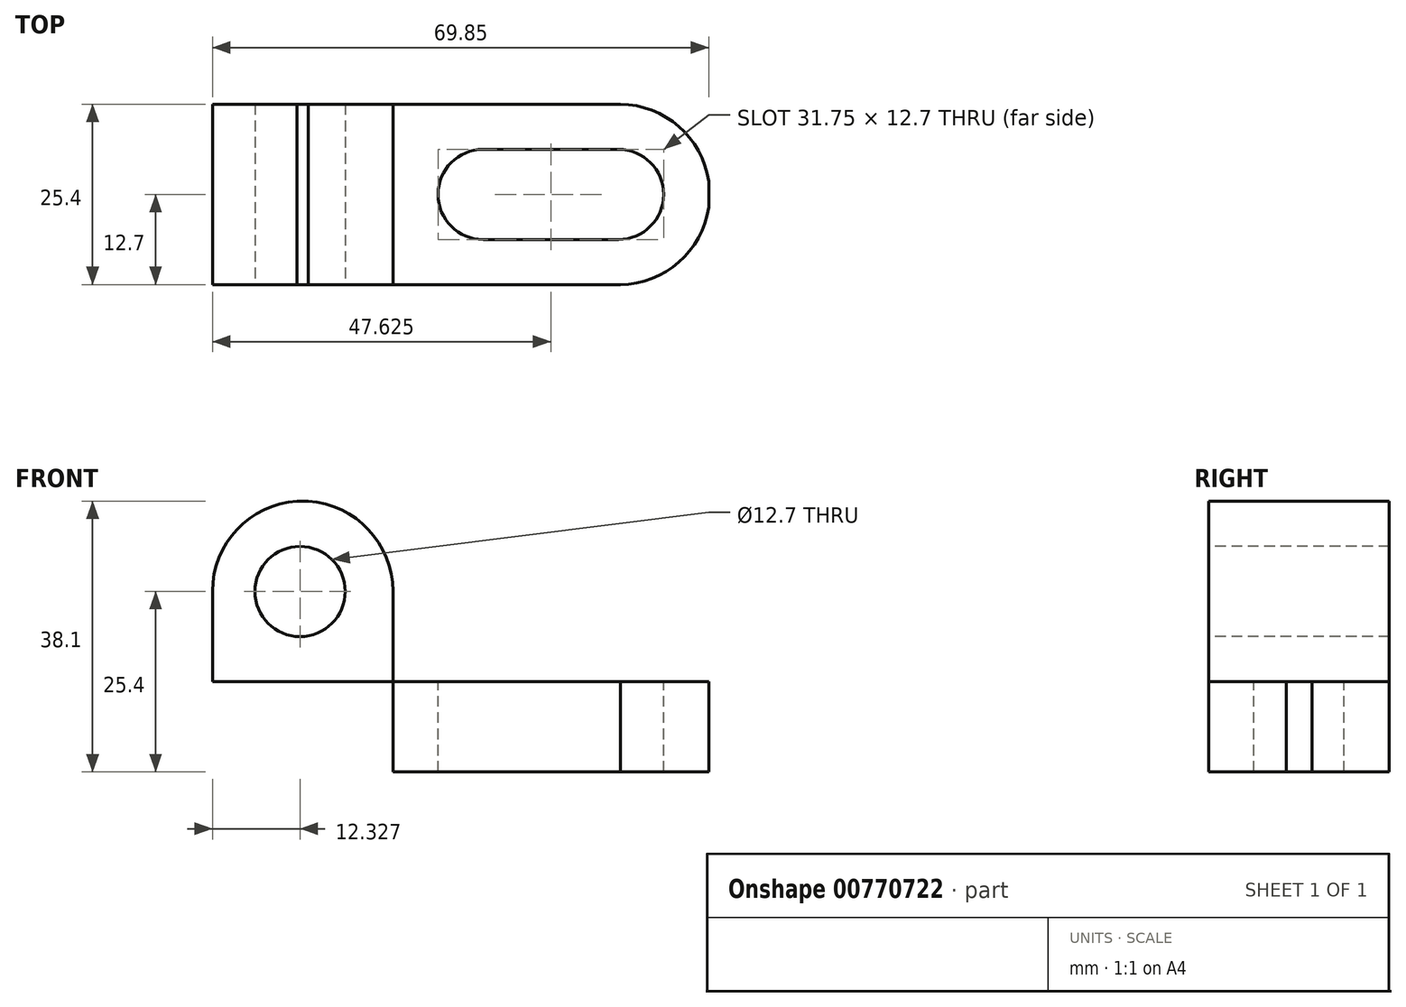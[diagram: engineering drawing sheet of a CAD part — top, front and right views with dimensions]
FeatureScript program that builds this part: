
annotation { "Feature Type Name" : "Feature", "Feature Type Description" : "" }
export const myFeature = defineFeature(function(context is Context, id is Id, definition is map)
    precondition{}
    {
        {
            var Q0;
            Q0=qCreatedBy(makeId("Front.planeOp"),FACE);
            var sketch = newSketch(context, id + "F0", { "sketchPlane" : qUnion([Q0])});
            skLineSegment(sketch, "E0.bottom", {"start": v(0, 0) * mm, "end": v(25.4, 0) * mm});
            skLineSegment(sketch, "E0.top", {"start": v(0, 38.1) * mm, "end": v(25.4, 38.1) * mm});
            skLineSegment(sketch, "E0.left", {"start": v(0, 0) * mm, "end": v(0, 38.1) * mm});
            skLineSegment(sketch, "E0.right", {"start": v(25.4, 0) * mm, "end": v(25.4, 38.1) * mm});
            skLineSegment(sketch, "E1.bottom", {"start": v(0, 0) * mm, "end": v(69.85, 0) * mm});
            skLineSegment(sketch, "E1.top", {"start": v(0, 12.7) * mm, "end": v(69.85, 12.7) * mm});
            skLineSegment(sketch, "E1.left", {"start": v(0, 0) * mm, "end": v(0, 12.7) * mm});
            skLineSegment(sketch, "E1.right", {"start": v(69.85, 0) * mm, "end": v(69.85, 12.7) * mm});
            skSolve(sketch);
        }
        {
            var Q0;
            {var subQ0=sQuery(id+"F0.wireOp",EDGE,"E0.top");Q0=makeQuery(id+"F0.imprint","IMPRINT",FACE,{"disambiguationData":[TD([[makeQuery(id+"F0.imprint","IMPRINT",EDGE,{"derivedFrom":subQ0}),-1.0]])]});}
            var Q1;
            {var subQ5=sQuery(id+"F0.wireOp",EDGE,"E1.left");Q1=makeQuery(id+"F0.imprint","IMPRINT",FACE,{"disambiguationData":[TD([[makeQuery(id+"F0.imprint","IMPRINT",EDGE,{"derivedFrom":subQ5}),-1.0]])]});}
            var Q2;
            {var subQ5=sQuery(id+"F0.wireOp",EDGE,"E1.right");Q2=makeQuery(id+"F0.imprint","IMPRINT",FACE,{"disambiguationData":[TD([[makeQuery(id+"F0.imprint","IMPRINT",EDGE,{"derivedFrom":subQ5}),1.0]])]});}
            extrude(context, id + "F1", {"entities" : qUnion([Q0, Q1, Q2]), "depth" : 25.4 * mm});
        }
        {
            var Q0;
            Q0=makeQuery(id+"F1.opExtrude","CAP_FACE",FACE,{"disambiguationData":[OSD([sQuery(id+"F0.wireOp",EDGE,"E0.top"),sQuery(id+"F0.wireOp",EDGE,"E0.left"),sQuery(id+"F0.wireOp",EDGE,"E0.right"),sQuery(id+"F0.wireOp",EDGE,"E1.bottom"),sQuery(id+"F0.wireOp",EDGE,"E1.top"),sQuery(id+"F0.wireOp",EDGE,"E1.left"),sQuery(id+"F0.wireOp",EDGE,"E1.right")])],"isStart":false});
            var sketch = newSketch(context, id + "F2", { "sketchPlane" : qUnion([Q0])});
            skCircle(sketch, "E2", {"center": v(12.33, 25.4) * mm, "radius": 6.35 * mm});
            skArc(sketch, "E3", {"start": v(25.4, 25.4) * mm, "mid": v(12.7, 38.12) * mm, "end": v(0, 25.4) * mm});
            skSolve(sketch);
        }
        {
            var Q0;
            Q0=qSketchRegion(id+"F2",true);
            var Q1;
            {var subQ0=sQuery(id+"F2.wireOp",EDGE,"E3");var subQ1=makeQuery(id+"F1.opExtrude","CAP_EDGE",EDGE,{"disambiguationData":[OSD([sQuery(id+"F0.wireOp",EDGE,"E0.right")])],"isStart":false});var subQ2=makeQuery(id+"F2.imprint","INTERSECT",VERTEX,{"derivedFrom":[subQ1,subQ0]});Q1=makeQuery(id+"F2.imprint","IMPRINT",FACE,{"disambiguationData":[TD([[makeQuery(id+"F2.imprint","IMPRINT",EDGE,{"disambiguationData":[TD([[subQ2,-1.0]])],"derivedFrom":subQ0}),-1.0]])]});}
            var Q2;
            {var subQ0=sQuery(id+"F2.wireOp",EDGE,"E3");var subQ3=makeQuery(id+"F1.opExtrude","CAP_EDGE",EDGE,{"disambiguationData":[OSD([sQuery(id+"F0.wireOp",EDGE,"E0.top")])],"isStart":false});var subQ4=makeQuery(id+"F2.imprint","INTERSECT",VERTEX,{"disambiguationData":[OD(1.0)],"derivedFrom":[subQ3,subQ0]});Q2=makeQuery(id+"F2.imprint","IMPRINT",FACE,{"disambiguationData":[TD([[makeQuery(id+"F2.imprint","IMPRINT",EDGE,{"disambiguationData":[TD([[subQ4,-1.0]])],"derivedFrom":subQ0}),-1.0]])]});}
            extrude(context, id + "F3", {"entities" : qUnion([Q0, Q1, Q2]), "operationType" : NewBodyOperationType.REMOVE, "oppositeDirection" : true, "depth" : 25.4 * mm});
        }
        {
            var Q0;
            Q0=makeQuery(id+"F1.opExtrude","SWEPT_FACE",FACE,{"disambiguationData":[OSD([sQuery(id+"F0.wireOp",EDGE,"E1.top")])]});
            var sketch = newSketch(context, id + "F4", { "sketchPlane" : qUnion([Q0])});
            skCircle(sketch, "E4", {"center": v(38.1, -12.7) * mm, "radius": 6.35 * mm});
            skCircle(sketch, "E5", {"center": v(57.15, -12.7) * mm, "radius": 6.35 * mm});
            skLineSegment(sketch, "E6", {"start": v(38.1, -19.05) * mm, "end": v(57.15, -19.05) * mm});
            skLineSegment(sketch, "E7", {"start": v(38.1, -6.35) * mm, "end": v(57.15, -6.35) * mm});
            skArc(sketch, "E8", {"start": v(57.15, -25.4) * mm, "mid": v(69.98, -12.7) * mm, "end": v(57.15, 0) * mm});
            skSolve(sketch);
        }
        {
            var Q0;
            {var subQ0=sQuery(id+"F4.wireOp",EDGE,"E4");var subQ1=makeQuery(id+"F4.imprint","INTERSECT",VERTEX,{"derivedFrom":[subQ0,sQuery(id+"F4.wireOp",EDGE,"E6")]});Q0=makeQuery(id+"F4.imprint","IMPRINT",FACE,{"disambiguationData":[TD([[makeQuery(id+"F4.imprint","IMPRINT",EDGE,{"disambiguationData":[TD([[subQ1,1.0]])],"derivedFrom":subQ0}),1.0]])]});}
            var Q1;
            {var subQ0=sQuery(id+"F4.wireOp",EDGE,"E6");Q1=makeQuery(id+"F4.imprint","IMPRINT",FACE,{"disambiguationData":[TD([[makeQuery(id+"F4.imprint","IMPRINT",EDGE,{"derivedFrom":subQ0}),1.0]])]});}
            var Q2;
            {var subQ0=sQuery(id+"F4.wireOp",EDGE,"E5");var subQ1=makeQuery(id+"F4.imprint","INTERSECT",VERTEX,{"derivedFrom":[subQ0,sQuery(id+"F4.wireOp",EDGE,"E6")]});Q2=makeQuery(id+"F4.imprint","IMPRINT",FACE,{"disambiguationData":[TD([[makeQuery(id+"F4.imprint","IMPRINT",EDGE,{"disambiguationData":[TD([[subQ1,1.0]])],"derivedFrom":subQ0}),1.0]])]});}
            var Q3;
            {var subQ0=sQuery(id+"F4.wireOp",EDGE,"E8");var subQ1=sQuery(id+"F0.wireOp",EDGE,"E1.top");var subQ4=makeQuery(id+"F1.opExtrude","CAP_EDGE",EDGE,{"disambiguationData":[OSD([subQ1])],"isStart":true});var subQ5=makeQuery(id+"F4.imprint","INTERSECT",VERTEX,{"disambiguationData":[OD(1.0)],"derivedFrom":[subQ4,subQ0]});Q3=makeQuery(id+"F4.imprint","IMPRINT",FACE,{"disambiguationData":[TD([[makeQuery(id+"F4.imprint","IMPRINT",EDGE,{"disambiguationData":[TD([[subQ5,1.0]])],"derivedFrom":subQ0}),-1.0]])]});}
            var Q4;
            {var subQ0=sQuery(id+"F4.wireOp",EDGE,"E8");var subQ1=sQuery(id+"F0.wireOp",EDGE,"E1.top");var subQ2=makeQuery(id+"F1.opExtrude","CAP_EDGE",EDGE,{"disambiguationData":[OSD([subQ1])],"isStart":false});var subQ3=makeQuery(id+"F4.imprint","INTERSECT",VERTEX,{"disambiguationData":[OD(1.0)],"derivedFrom":[subQ2,subQ0]});Q4=makeQuery(id+"F4.imprint","IMPRINT",FACE,{"disambiguationData":[TD([[makeQuery(id+"F4.imprint","IMPRINT",EDGE,{"disambiguationData":[TD([[subQ3,-1.0]])],"derivedFrom":subQ0}),-1.0]])]});}
            extrude(context, id + "F5", {"entities" : qUnion([Q0, Q1, Q2, Q3, Q4]), "operationType" : NewBodyOperationType.REMOVE, "oppositeDirection" : true, "depth" : 25.4 * mm});
        }
    });
